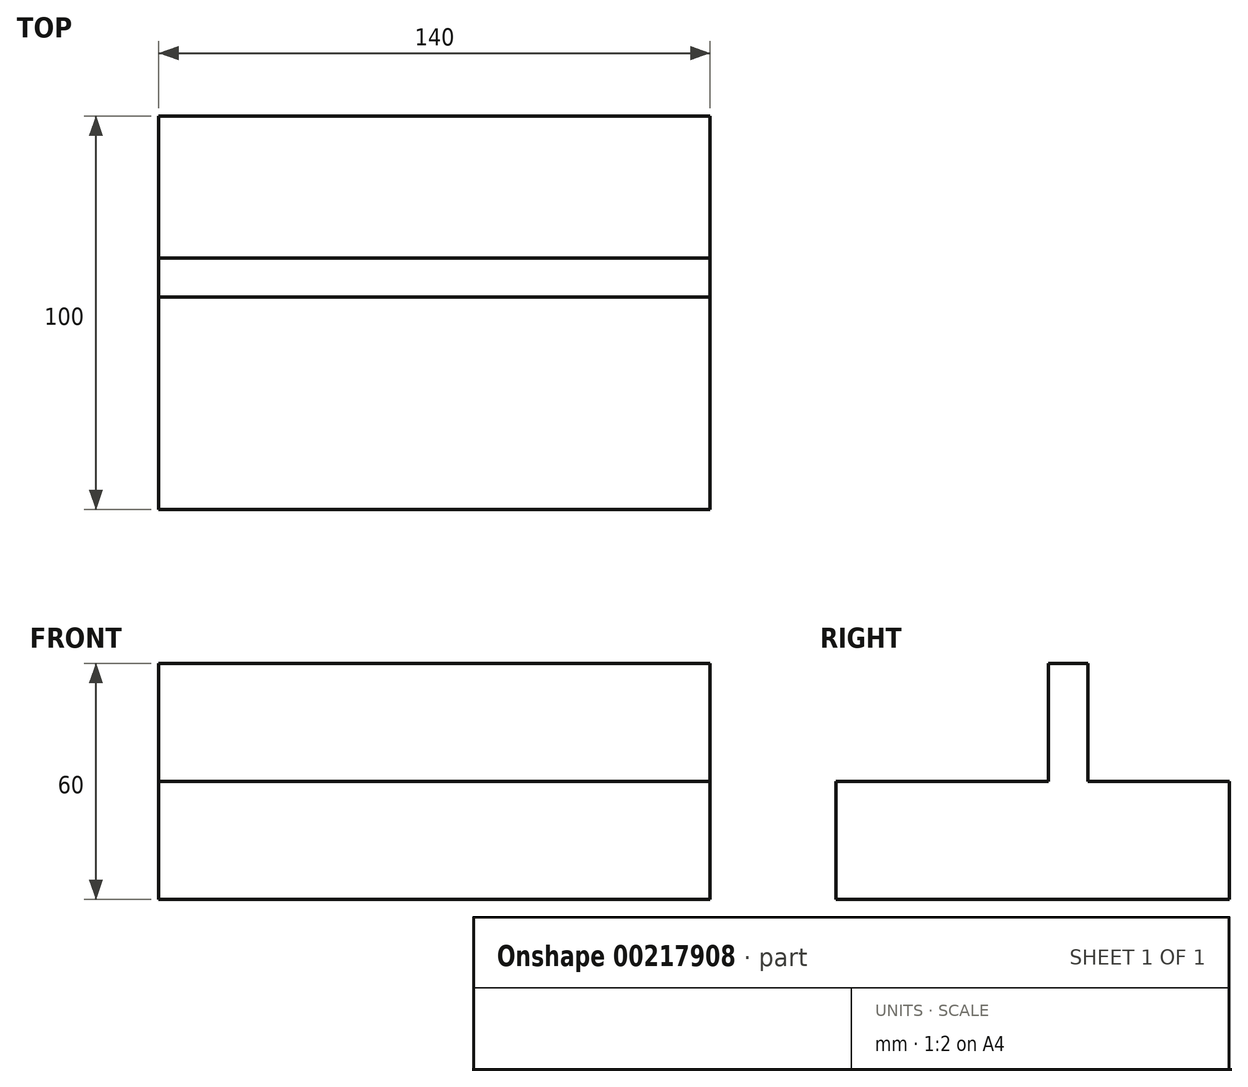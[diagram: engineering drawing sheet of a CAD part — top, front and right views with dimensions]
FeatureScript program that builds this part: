
annotation { "Feature Type Name" : "Feature", "Feature Type Description" : "" }
export const myFeature = defineFeature(function(context is Context, id is Id, definition is map)
    precondition{}
    {
        {
            var Q0;
            Q0=qCreatedBy(makeId("Right.planeOp"),FACE);
            var sketch = newSketch(context, id + "F0", { "sketchPlane" : qUnion([Q0])});
            skLineSegment(sketch, "E0", {"start": v(-34.87, -14.45) * mm, "end": v(-34.87, 15.55) * mm});
            skLineSegment(sketch, "E1", {"start": v(-34.87, 15.55) * mm, "end": v(19.13, 15.55) * mm});
            skLineSegment(sketch, "E2", {"start": v(19.13, 15.55) * mm, "end": v(19.13, 45.55) * mm});
            skLineSegment(sketch, "E3", {"start": v(19.13, 45.55) * mm, "end": v(29.13, 45.55) * mm});
            skLineSegment(sketch, "E4", {"start": v(65.13, -14.45) * mm, "end": v(-34.87, -14.45) * mm});
            skLineSegment(sketch, "E5", {"start": v(29.13, 45.55) * mm, "end": v(29.13, 15.55) * mm});
            skLineSegment(sketch, "E6", {"start": v(29.13, 15.55) * mm, "end": v(65.13, 15.55) * mm});
            skLineSegment(sketch, "E7", {"start": v(65.13, 15.55) * mm, "end": v(65.13, -14.45) * mm});
            skSolve(sketch);
        }
        {
            var Q0;
            Q0=makeQuery(id+"F0.imprint","IMPRINT",FACE,{"disambiguationData":[TD([[makeQuery(id+"F0.imprint","IMPRINT",EDGE,{"derivedFrom":sQuery(id+"F0.wireOp",EDGE,"E0")}),-1.0]])]});
            extrude(context, id + "F1", {"entities" : qUnion([Q0]), "depth" : 140 * mm});
        }
    });
